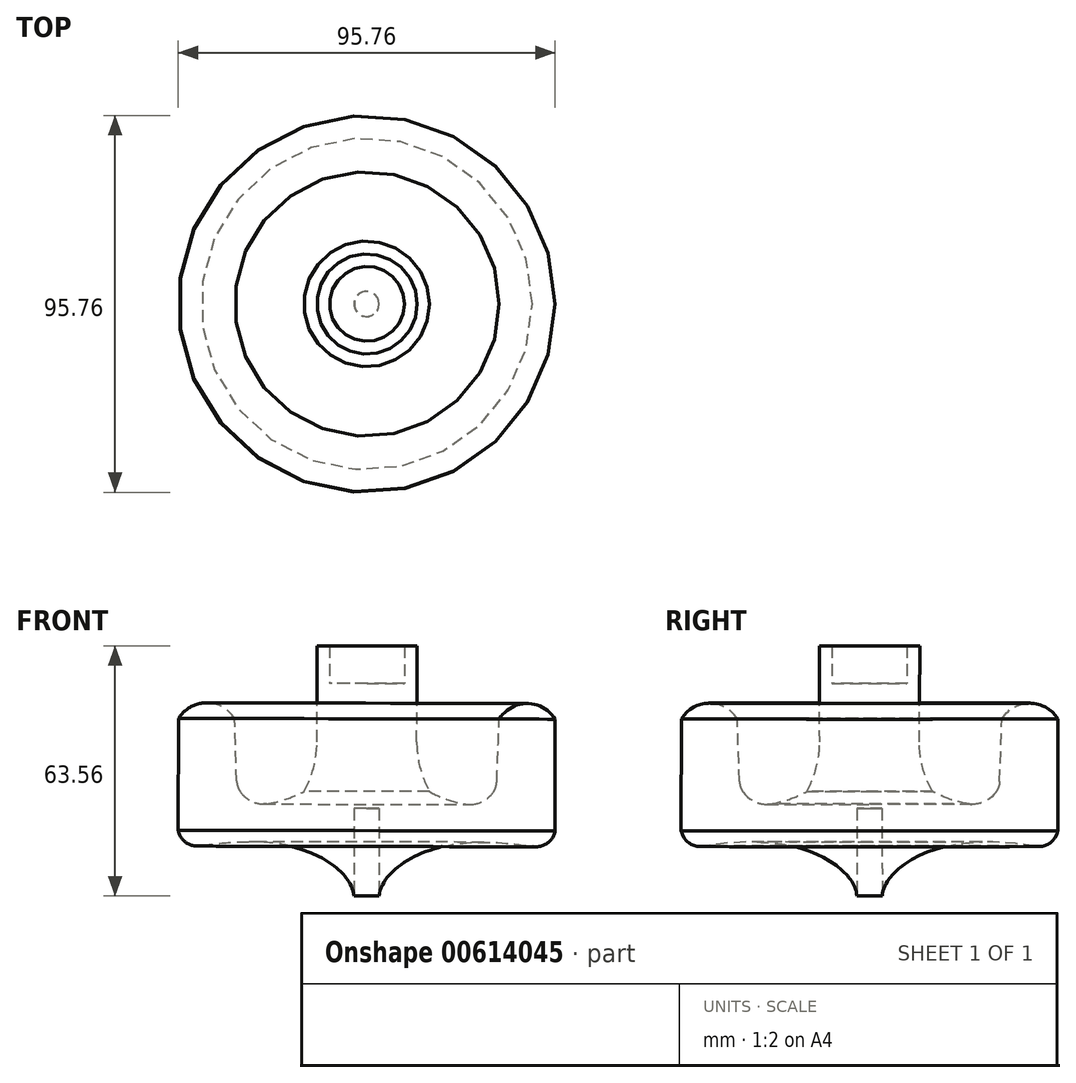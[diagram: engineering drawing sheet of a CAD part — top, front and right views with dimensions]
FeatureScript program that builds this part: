
annotation { "Feature Type Name" : "Feature", "Feature Type Description" : "" }
export const myFeature = defineFeature(function(context is Context, id is Id, definition is map)
    precondition{}
    {
        {
            var Q0;
            Q0=qCreatedBy(makeId("Front.planeOp"),FACE);
            var sketch = newSketch(context, id + "F0", { "sketchPlane" : qUnion([Q0])});
            skArc(sketch, "E0", {"start": v(47.8, 44.93) * mm, "mid": v(40.7, 48.91) * mm, "end": v(33.6, 44.93) * mm});
            skArc(sketch, "E1", {"start": v(15.89, 26.53) * mm, "mid": v(20.63, 24.46) * mm, "end": v(25.67, 23.27) * mm});
            skArc(sketch, "E2", {"start": v(12.63, 39.1) * mm, "mid": v(13.47, 32.61) * mm, "end": v(15.89, 26.53) * mm});
            skFitSpline(sketch, "E3", {"points": [v(3.1, 0) * mm, v(13.42, 10.66) * mm, v(44.42, 12.17) * mm], "startDerivative": vector(1.98, 30.62) * mm, "endDerivative": vector(64.45, -11.84) * mm});
            skLineSegment(sketch, "E4", {"start": v(33.6, 44.93) * mm, "end": v(32.95, 28) * mm});
            skArc(sketch, "E5", {"start": v(25.67, 23.27) * mm, "mid": v(30.08, 24.45) * mm, "end": v(32.95, 28) * mm});
            skLineSegment(sketch, "E6", {"start": v(-0.07, 22.23) * mm, "end": v(3.1, 22.23) * mm});
            skLineSegment(sketch, "E7", {"start": v(3.1, 0) * mm, "end": v(3.1, 22.23) * mm});
            skLineSegment(sketch, "E8", {"start": v(12.75, 63.5) * mm, "end": v(9.52, 63.5) * mm});
            skLineSegment(sketch, "E9", {"start": v(9.52, 63.5) * mm, "end": v(9.52, 53.98) * mm});
            skLineSegment(sketch, "E10", {"start": v(9.52, 53.98) * mm, "end": v(0, 53.98) * mm});
            skLineSegment(sketch, "E11", {"start": v(0, 53.98) * mm, "end": v(-0.07, 22.23) * mm});
            skPoint(sketch, "E12.third.point", {"position": v(47.8, 16.51) * mm});
            skArc(sketch, "E13", {"start": v(42.01, 12.58) * mm, "mid": v(45.71, 13.36) * mm, "end": v(47.8, 16.51) * mm});
            skLineSegment(sketch, "E14.trimOffspring", {"start": v(42.01, 12.58) * mm, "end": v(42.01, 12.58) * mm});
            skLineSegment(sketch, "E15", {"start": v(47.8, 44.93) * mm, "end": v(47.8, 16.51) * mm});
            skLineSegment(sketch, "E16", {"start": v(12.75, 63.5) * mm, "end": v(12.63, 39.1) * mm});
            skSolve(sketch);
        }
        {
            var Q0;
            Q0 = qSketchRegion(id + "F0", true);
            var Q1;
            Q1=sQuery(id+"F0.wireOp",EDGE,"E11");
            revolve(context, id + "F1", {"entities" : qUnion([Q0]), "axis" : qUnion([Q1]), "revolveType" : RevolveType.FULL});
        }
        {
            var Q0;
            Q0=makeQuery(id+"F1.opRevolve","SWEPT_FACE",FACE,{"disambiguationData":[OSD([sQuery(id+"F0.wireOp",EDGE,"DOEBhLHd-Dio7-r6yo-HJs7-0gwbalOT1rXP")])]});
            var Q1;
            Q1=makeQuery(id+"F1.opRevolve","SWEPT_FACE",FACE,{"disambiguationData":[OSD([sQuery(id+"F0.wireOp",EDGE,"E5")])]});
            fillet(context, id + "F2", {"entities" : qUnion([Q0, Q1]), "radius" : 5.08 * mm, "tangentPropagation" : true, "allowEdgeOverflow" : false});
        }
    });
